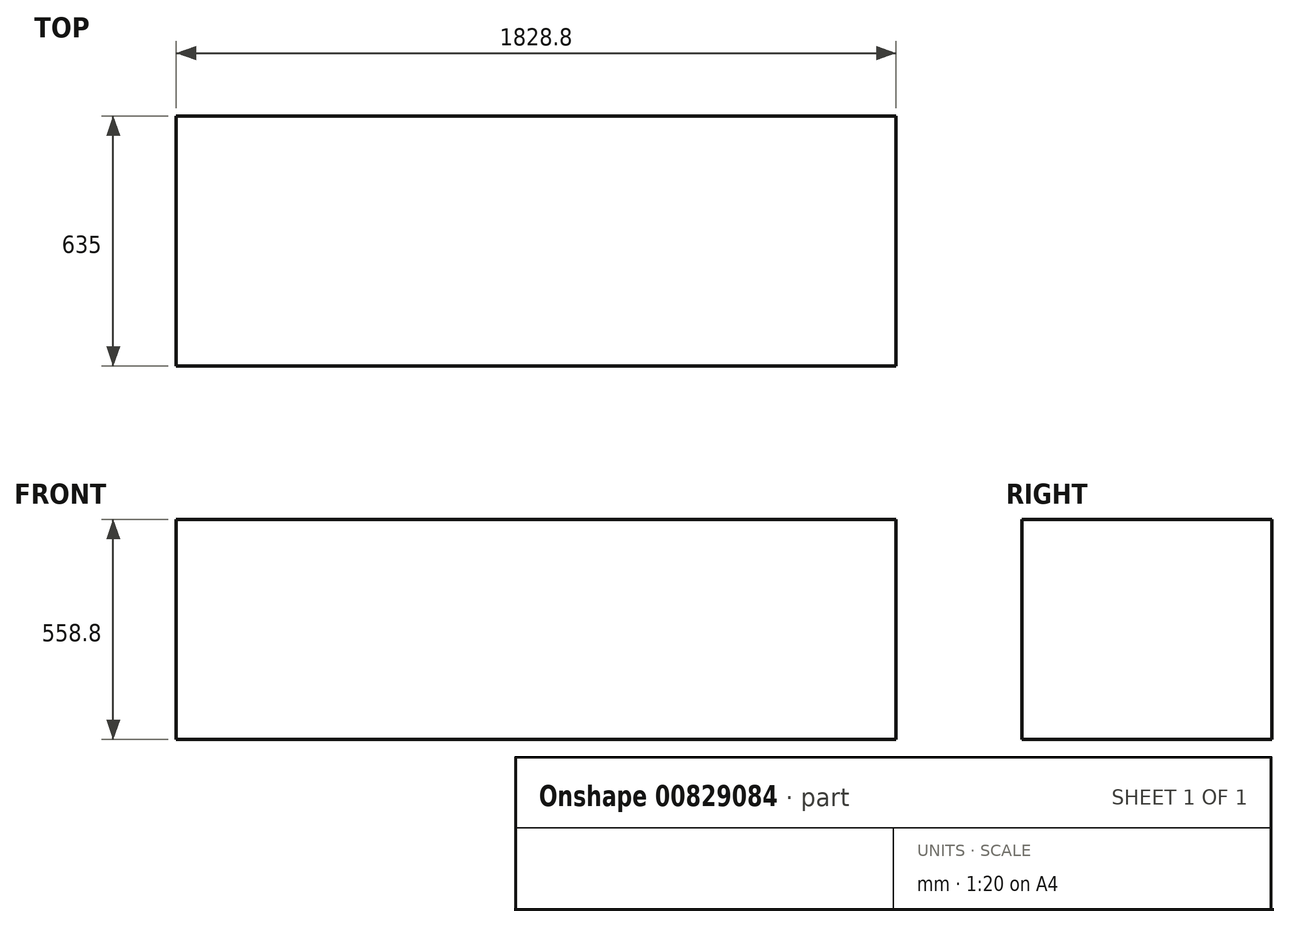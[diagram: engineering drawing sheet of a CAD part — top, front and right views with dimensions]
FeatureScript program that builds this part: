
annotation { "Feature Type Name" : "Feature", "Feature Type Description" : "" }
export const myFeature = defineFeature(function(context is Context, id is Id, definition is map)
    precondition{}
    {
        {
            var Q0;
            Q0=qCreatedBy(makeId("Front.planeOp"),FACE);
            var sketch = newSketch(context, id + "F0", { "sketchPlane" : qUnion([Q0])});
            skLineSegment(sketch, "E0.bottom", {"start": v(914.4, -279.4) * mm, "end": v(-914.4, -279.4) * mm});
            skLineSegment(sketch, "E0.top", {"start": v(914.4, 279.4) * mm, "end": v(-914.4, 279.4) * mm});
            skLineSegment(sketch, "E0.left", {"start": v(914.4, -279.4) * mm, "end": v(914.4, 279.4) * mm});
            skLineSegment(sketch, "E0.right", {"start": v(-914.4, -279.4) * mm, "end": v(-914.4, 279.4) * mm});
            skPoint(sketch, "E0.middle", {"position": v(0, 0) * mm});
            skSolve(sketch);
        }
        {
            var Q0;
            Q0 = qSketchRegion(id + "F0", true);
            extrude(context, id + "F1", {"entities" : qUnion([Q0]), "depth" : 635 * mm, "offsetDistance" : 25.4 * mm});
        }
    });
